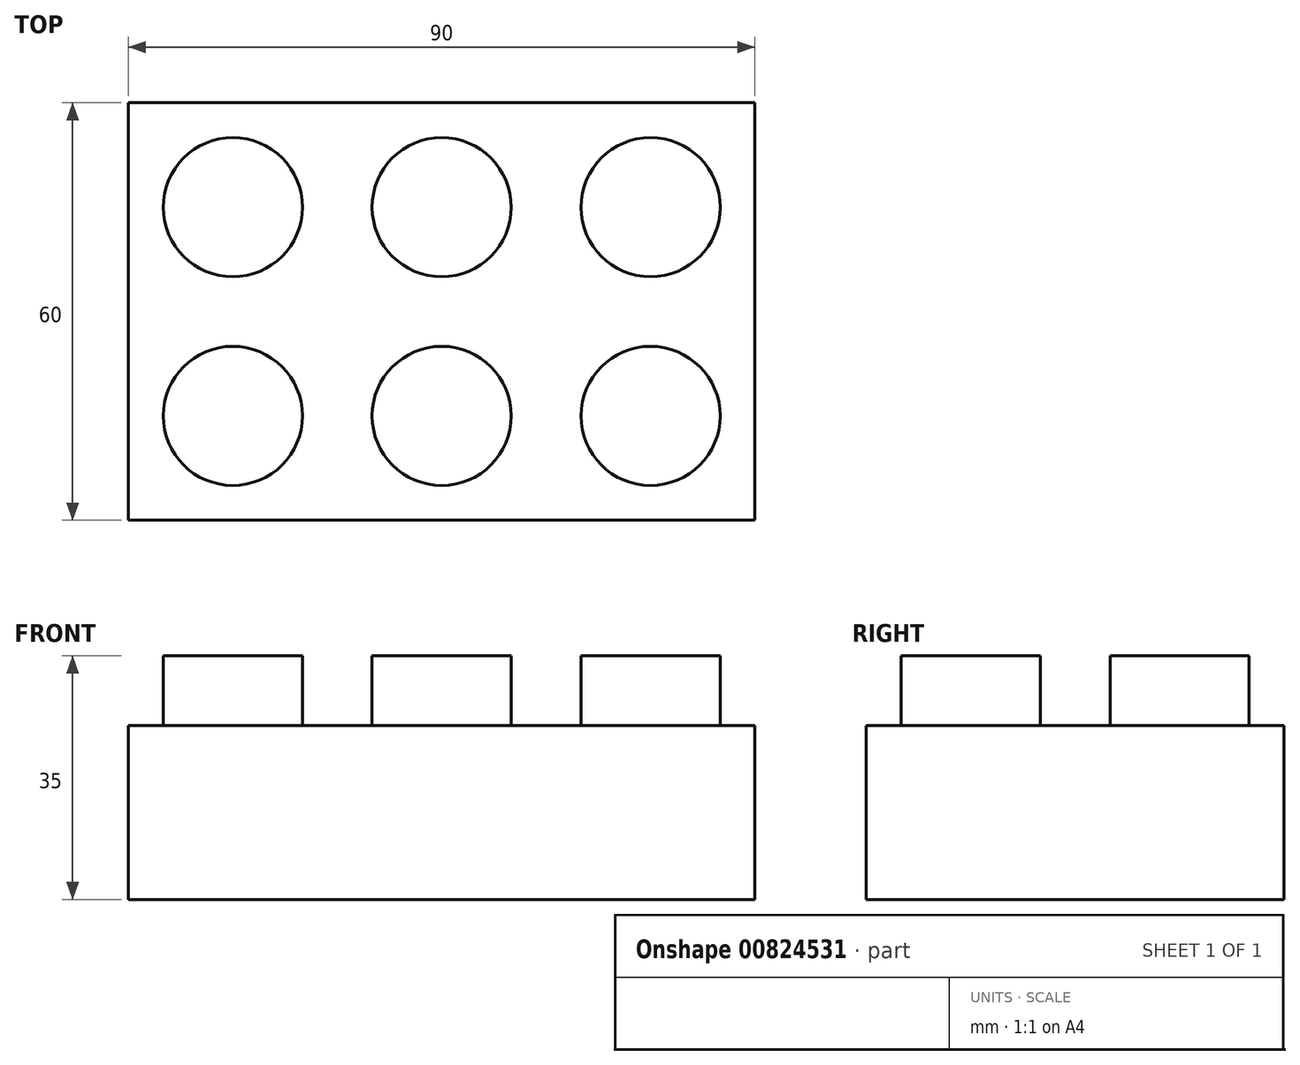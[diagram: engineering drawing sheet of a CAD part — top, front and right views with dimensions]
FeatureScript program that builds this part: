
annotation { "Feature Type Name" : "Feature", "Feature Type Description" : "" }
export const myFeature = defineFeature(function(context is Context, id is Id, definition is map)
    precondition{}
    {
        {
            var Q0;
            Q0=qCreatedBy(makeId("Top.planeOp"),FACE);
            var sketch = newSketch(context, id + "F0", { "sketchPlane" : qUnion([Q0])});
            skLineSegment(sketch, "E0.bottom", {"start": v(-38.9, 29.34) * mm, "end": v(51.1, 29.34) * mm});
            skLineSegment(sketch, "E0.top", {"start": v(-38.9, -30.66) * mm, "end": v(51.1, -30.66) * mm});
            skLineSegment(sketch, "E0.left", {"start": v(-38.9, 29.34) * mm, "end": v(-38.9, -30.66) * mm});
            skLineSegment(sketch, "E0.right", {"start": v(51.1, 29.34) * mm, "end": v(51.1, -30.66) * mm});
            skSolve(sketch);
        }
        {
            var Q0;
            Q0=makeQuery(id+"F0.imprint","IMPRINT",FACE,{"disambiguationData":[TD([[makeQuery(id+"F0.imprint","IMPRINT",EDGE,{"derivedFrom":sQuery(id+"F0.wireOp",EDGE,"E0.bottom")}),-1.0]])]});
            extrude(context, id + "F1", {"entities" : qUnion([Q0]), "depth" : 25 * mm, "offsetDistance" : 25 * mm});
        }
        {
            var Q0;
            Q0=makeQuery(id+"F1.opExtrude","CAP_FACE",FACE,{"disambiguationData":[OSD([sQuery(id+"F0.wireOp",EDGE,"E0.bottom"),sQuery(id+"F0.wireOp",EDGE,"E0.top"),sQuery(id+"F0.wireOp",EDGE,"E0.left"),sQuery(id+"F0.wireOp",EDGE,"E0.right")])],"isStart":false});
            var sketch = newSketch(context, id + "F2", { "sketchPlane" : qUnion([Q0])});
            skCircle(sketch, "E1", {"center": v(-23.9, 14.34) * mm, "radius": 10 * mm});
            skCircle(sketch, "E2", {"center": v(6.1, 14.34) * mm, "radius": 10 * mm});
            skCircle(sketch, "E3", {"center": v(-23.9, -15.66) * mm, "radius": 10 * mm});
            skCircle(sketch, "E4", {"center": v(6.1, -15.66) * mm, "radius": 10 * mm});
            skCircle(sketch, "E5", {"center": v(36.1, 14.34) * mm, "radius": 10 * mm});
            skCircle(sketch, "E6", {"center": v(36.1, -15.66) * mm, "radius": 10 * mm});
            skSolve(sketch);
        }
        {
            var Q0;
            Q0=makeQuery(id+"F2.imprint","IMPRINT",FACE,{"disambiguationData":[TD([[makeQuery(id+"F2.imprint","IMPRINT",EDGE,{"derivedFrom":sQuery(id+"F2.wireOp",EDGE,"E1")}),1.0]])]});
            var Q1;
            Q1=makeQuery(id+"F2.imprint","IMPRINT",FACE,{"disambiguationData":[TD([[makeQuery(id+"F2.imprint","IMPRINT",EDGE,{"derivedFrom":sQuery(id+"F2.wireOp",EDGE,"E2")}),1.0]])]});
            var Q2;
            Q2=makeQuery(id+"F2.imprint","IMPRINT",FACE,{"disambiguationData":[TD([[makeQuery(id+"F2.imprint","IMPRINT",EDGE,{"derivedFrom":sQuery(id+"F2.wireOp",EDGE,"E5")}),1.0]])]});
            var Q3;
            Q3=makeQuery(id+"F2.imprint","IMPRINT",FACE,{"disambiguationData":[TD([[makeQuery(id+"F2.imprint","IMPRINT",EDGE,{"derivedFrom":sQuery(id+"F2.wireOp",EDGE,"E6")}),1.0]])]});
            var Q4;
            Q4=makeQuery(id+"F2.imprint","IMPRINT",FACE,{"disambiguationData":[TD([[makeQuery(id+"F2.imprint","IMPRINT",EDGE,{"derivedFrom":sQuery(id+"F2.wireOp",EDGE,"E4")}),1.0]])]});
            var Q5;
            Q5=makeQuery(id+"F2.imprint","IMPRINT",FACE,{"disambiguationData":[TD([[makeQuery(id+"F2.imprint","IMPRINT",EDGE,{"derivedFrom":sQuery(id+"F2.wireOp",EDGE,"E3")}),1.0]])]});
            extrude(context, id + "F3", {"entities" : qUnion([Q0, Q1, Q2, Q3, Q4, Q5]), "operationType" : NewBodyOperationType.ADD, "depth" : 10 * mm, "offsetDistance" : 25 * mm});
        }
    });
